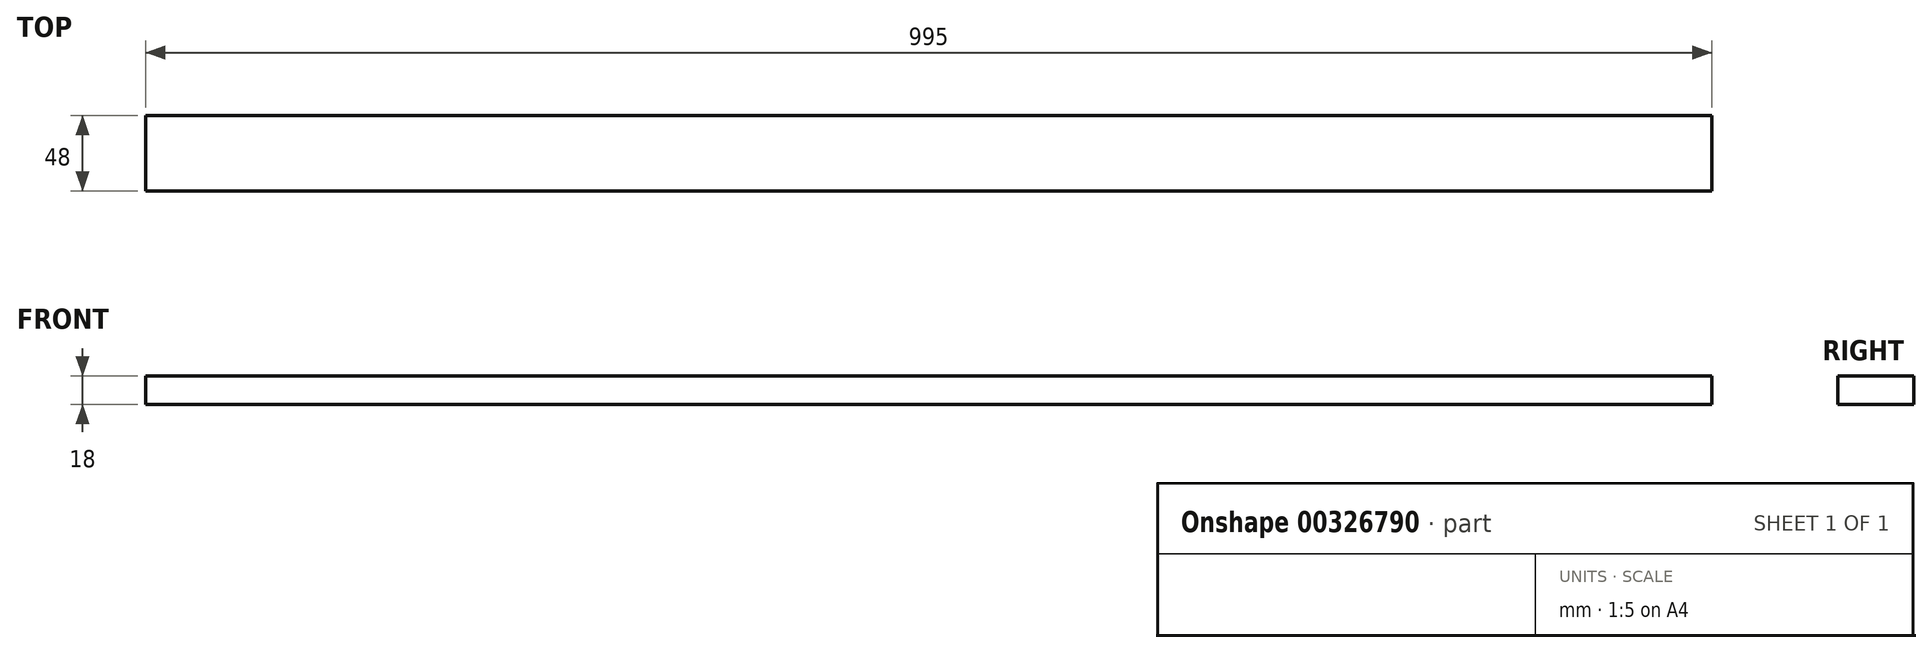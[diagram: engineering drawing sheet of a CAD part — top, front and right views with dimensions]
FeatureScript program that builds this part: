
annotation { "Feature Type Name" : "Feature", "Feature Type Description" : "" }
export const myFeature = defineFeature(function(context is Context, id is Id, definition is map)
    precondition{}
    {
        {
            var Q0;
            Q0=qCreatedBy(makeId("Top.planeOp"),FACE);
            var sketch = newSketch(context, id + "F0", { "sketchPlane" : qUnion([Q0])});
            skLineSegment(sketch, "E0.bottom", {"start": v(0, 0) * mm, "end": v(995, 0) * mm});
            skLineSegment(sketch, "E0.top", {"start": v(0, 48) * mm, "end": v(995, 48) * mm});
            skLineSegment(sketch, "E0.left", {"start": v(0, 0) * mm, "end": v(0, 48) * mm});
            skLineSegment(sketch, "E0.right", {"start": v(995, 0) * mm, "end": v(995, 48) * mm});
            skSolve(sketch);
        }
        {
            var Q0;
            Q0=qSketchRegion(id+"F0",true);
            extrude(context, id + "F1", {"entities" : qUnion([Q0]), "depth" : 18 * mm});
        }
    });
